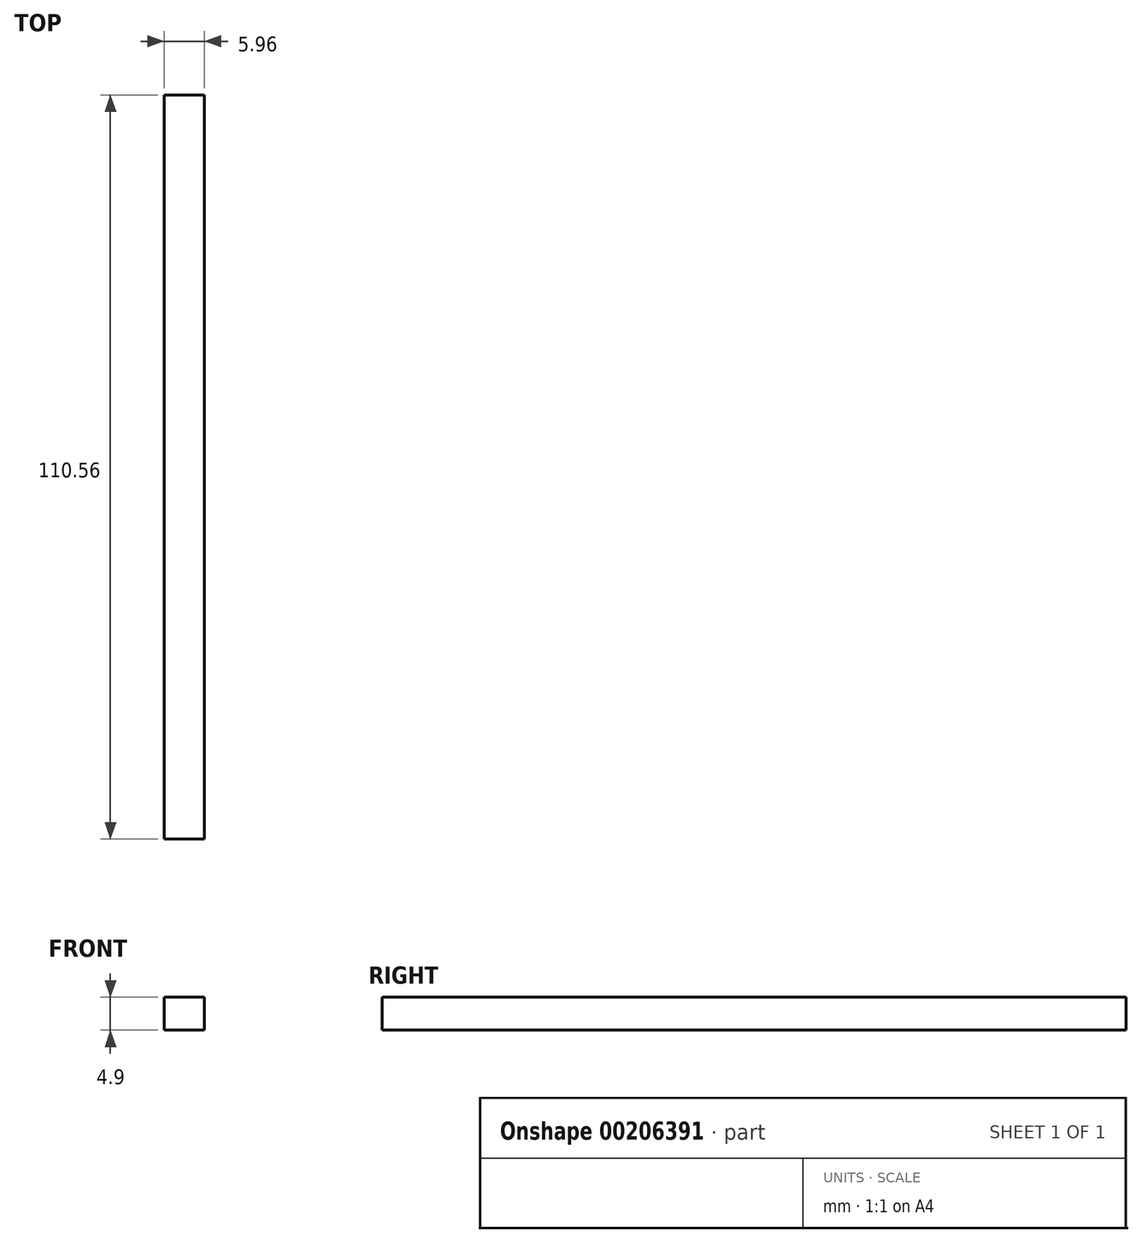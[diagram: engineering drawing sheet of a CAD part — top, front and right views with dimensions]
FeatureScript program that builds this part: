
annotation { "Feature Type Name" : "Feature", "Feature Type Description" : "" }
export const myFeature = defineFeature(function(context is Context, id is Id, definition is map)
    precondition{}
    {
        {
            var Q0;
            Q0=qCreatedBy(makeId("Top.planeOp"),FACE);
            var sketch = newSketch(context, id + "F0", { "sketchPlane" : qUnion([Q0])});
            skLineSegment(sketch, "E0", {"start": v(-66.45, 46.34) * mm, "end": v(-66.45, -64.22) * mm});
            skLineSegment(sketch, "E1", {"start": v(-66.45, -64.22) * mm, "end": v(-60.5, -64.22) * mm});
            skLineSegment(sketch, "E2", {"start": v(-60.5, -64.22) * mm, "end": v(-60.5, 46.34) * mm});
            skLineSegment(sketch, "E3", {"start": v(-60.5, 46.34) * mm, "end": v(-66.45, 46.34) * mm});
            skSolve(sketch);
        }
        {
            var Q0;
            Q0=makeQuery(id+"F0.imprint","IMPRINT",FACE,{"disambiguationData":[TD([[makeQuery(id+"F0.imprint","IMPRINT",EDGE,{"derivedFrom":sQuery(id+"F0.wireOp",EDGE,"E0")}),1.0]])]});
            extrude(context, id + "F1", {"entities" : qUnion([Q0]), "depth" : 4.9 * mm});
        }
    });
